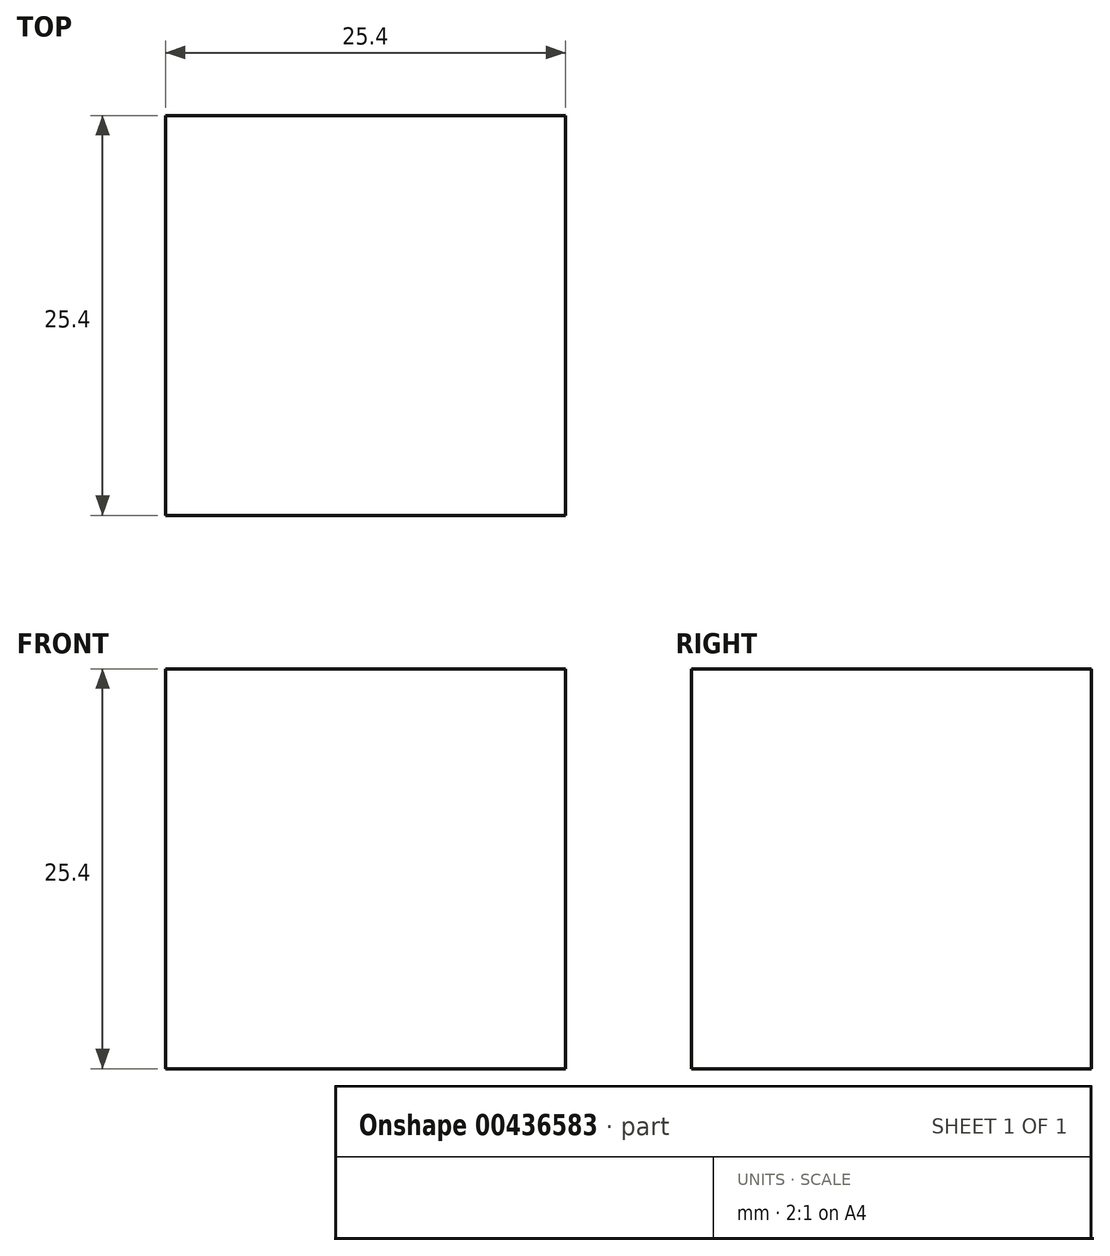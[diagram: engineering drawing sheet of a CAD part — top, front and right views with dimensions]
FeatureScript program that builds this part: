
annotation { "Feature Type Name" : "Feature", "Feature Type Description" : "" }
export const myFeature = defineFeature(function(context is Context, id is Id, definition is map)
    precondition{}
    {
        {
            var Q0;
            Q0=qCreatedBy(makeId("Front.planeOp"),FACE);
            var sketch = newSketch(context, id + "F0", { "sketchPlane" : qUnion([Q0])});
            skLineSegment(sketch, "E0.bottom", {"start": v(12.7, -12.7) * mm, "end": v(-12.7, -12.7) * mm});
            skLineSegment(sketch, "E0.top", {"start": v(12.7, 12.7) * mm, "end": v(-12.7, 12.7) * mm});
            skLineSegment(sketch, "E0.left", {"start": v(12.7, -12.7) * mm, "end": v(12.7, 12.7) * mm});
            skLineSegment(sketch, "E0.right", {"start": v(-12.7, -12.7) * mm, "end": v(-12.7, 12.7) * mm});
            skPoint(sketch, "E0.middle", {"position": v(0, 0) * mm});
            skSolve(sketch);
        }
        {
            var Q0;
            Q0=makeQuery(id+"F0.imprint","IMPRINT",FACE,{"disambiguationData":[TD([[makeQuery(id+"F0.imprint","IMPRINT",EDGE,{"derivedFrom":sQuery(id+"F0.wireOp",EDGE,"E0.bottom")}),-1.0]])]});
            extrude(context, id + "F1", {"entities" : qUnion([Q0]), "depth" : 25.4 * mm});
        }
    });
